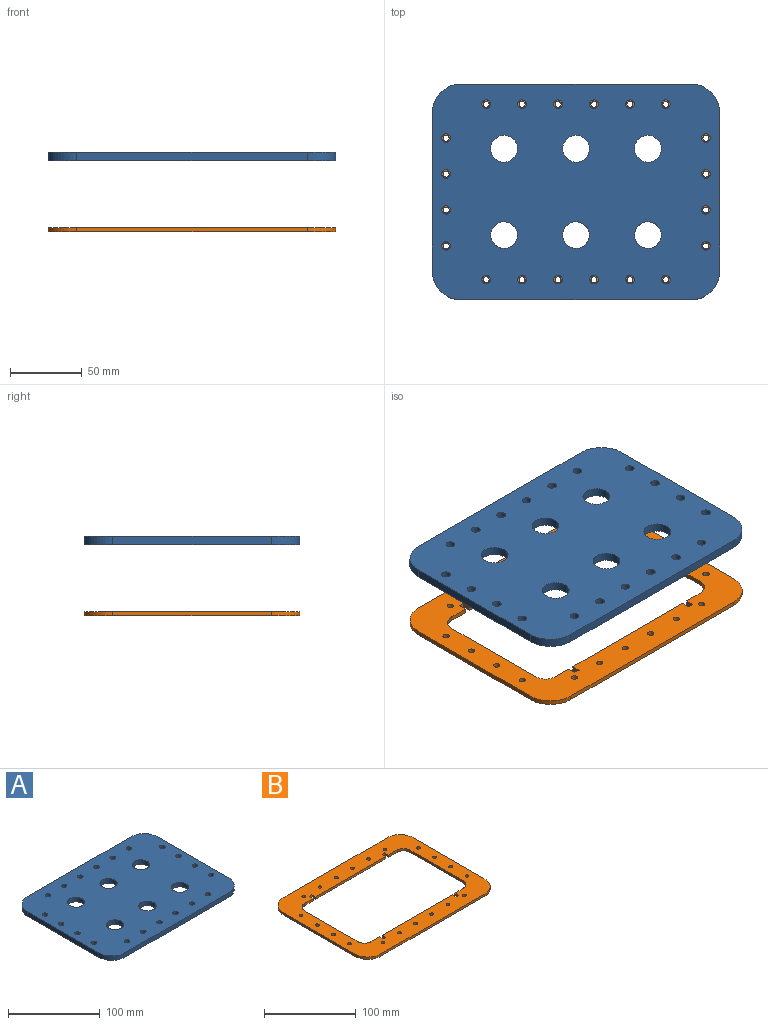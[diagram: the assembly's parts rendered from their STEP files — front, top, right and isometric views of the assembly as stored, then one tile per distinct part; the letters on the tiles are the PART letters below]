
ASSEMBLY  parts=2 mates=1
PART A: 36 faces, bbox 200x150x6 mm
  f0: cylinder r=20mm len=20mm, axis (0,0,1), area 188.5mm2, adj f1,f24,f34,f35
  f1: plane 110x6mm, normal (1,0,0), area 660mm2, adj f0,f2,f34,f35
  f2: cylinder r=20mm len=20mm, axis (0,0,1), area 188.5mm2, adj f1,f3,f34,f35
  f3: plane 160x6mm, normal (0,1,0), area 960mm2, adj f2,f4,f34,f35
  f4: cylinder r=20mm len=20mm, axis (0,0,1), area 188.5mm2, adj f3,f5,f34,f35
  f5: plane 110x6mm, normal (-1,0,0), area 660mm2, adj f4,f6,f34,f35
  f6: cylinder r=20mm len=20mm, axis (0,0,1), area 188.5mm2, adj f5,f24,f34,f35
  f7: cylinder r=3mm len=6mm, axis (0,0,1), area 113.1mm2, adj f34,f35
  f8: cylinder r=9.3mm len=18.6mm, axis (0,0,1), area 350.6mm2, adj f34,f35
  f9: cylinder r=3mm len=6mm, axis (0,0,1), area 113.1mm2, adj f34,f35
  f10: cylinder r=9.3mm len=18.6mm, axis (0,0,1), area 350.6mm2, adj f34,f35
  f11: cylinder r=9.3mm len=18.6mm, axis (0,0,1), area 350.6mm2, adj f34,f35
  f12: cylinder r=3mm len=6mm, axis (0,0,1), area 113.1mm2, adj f34,f35
  f13: cylinder r=3mm len=6mm, axis (0,0,1), area 113.1mm2, adj f34,f35
  f14: cylinder r=3mm len=6mm, axis (0,0,1), area 113.1mm2, adj f34,f35
  f15: cylinder r=3mm len=6mm, axis (0,0,1), area 113.1mm2, adj f34,f35
  f16: cylinder r=3mm len=6mm, axis (0,0,1), area 113.1mm2, adj f34,f35
  f17: cylinder r=3mm len=6mm, axis (0,0,1), area 113.1mm2, adj f34,f35
  f18: cylinder r=9.3mm len=18.6mm, axis (0,0,1), area 350.6mm2, adj f34,f35
  f19: cylinder r=3mm len=6mm, axis (0,0,1), area 113.1mm2, adj f34,f35
  f20: cylinder r=3mm len=6mm, axis (0,0,1), area 113.1mm2, adj f34,f35
  f21: cylinder r=3mm len=6mm, axis (0,0,1), area 113.1mm2, adj f34,f35
  f22: cylinder r=3mm len=6mm, axis (0,0,1), area 113.1mm2, adj f34,f35
  f23: cylinder r=3mm len=6mm, axis (0,0,1), area 113.1mm2, adj f34,f35
  f24: plane 160x6mm, normal (0,-1,0), area 960mm2, adj f0,f6,f34,f35
  f25: cylinder r=9.3mm len=18.6mm, axis (0,0,1), area 350.6mm2, adj f34,f35
  f26: cylinder r=3mm len=6mm, axis (0,0,1), area 113.1mm2, adj f34,f35
  f27: cylinder r=3mm len=6mm, axis (0,0,1), area 113.1mm2, adj f34,f35
  f28: cylinder r=3mm len=6mm, axis (0,0,1), area 113.1mm2, adj f34,f35
  f29: cylinder r=9.3mm len=18.6mm, axis (0,0,1), area 350.6mm2, adj f34,f35
  f30: cylinder r=3mm len=6mm, axis (0,0,1), area 113.1mm2, adj f34,f35
  f31: cylinder r=3mm len=6mm, axis (0,0,1), area 113.1mm2, adj f34,f35
  f32: cylinder r=3mm len=6mm, axis (0,0,1), area 113.1mm2, adj f34,f35
  f33: cylinder r=3mm len=6mm, axis (0,0,1), area 113.1mm2, adj f34,f35
  f34: plane 200x150mm, normal (0,0,1), area 27460.9mm2, adj f0,f1,f2,f3,f4,f5,f6,f7
  f35: plane 200x150mm, normal (0,0,-1), area 27460.9mm2, adj f0,f1,f2,f3,f4,f5,f6,f7
PART B: 54 faces, bbox 200x150x3 mm
  f0: plane 13x3mm, normal (0,1,0), area 39mm2, adj f1,f35,f52,f53
  f1: plane 6x3mm, normal (-1,0,0), area 18mm2, adj f0,f2,f52,f53
  f2: plane 4x3mm, normal (0,1,0), area 12mm2, adj f1,f3,f52,f53
  f3: plane 6x3mm, normal (1,0,0), area 18mm2, adj f2,f4,f52,f53
  f4: plane 108x3mm, normal (0,1,0), area 324mm2, adj f3,f5,f52,f53
  f5: plane 6x3mm, normal (-1,0,0), area 18mm2, adj f4,f6,f52,f53
  f6: plane 4x3mm, normal (0,1,0), area 12mm2, adj f5,f7,f52,f53
  f7: plane 6x3mm, normal (1,0,0), area 18mm2, adj f6,f8,f52,f53
  f8: plane 13x3mm, normal (0,1,0), area 39mm2, adj f7,f9,f52,f53
  f9: cylinder r=10mm len=10mm, axis (0,0,-1), area 47.1mm2, adj f8,f10,f52,f53
  f10: plane 81.95x3mm, normal (1,0,0), area 245.9mm2, adj f9,f11,f52,f53
  f11: cylinder r=10mm len=10mm, axis (0,0,-1), area 47.1mm2, adj f10,f12,f52,f53
  f12: plane 13x3mm, normal (0,-1,0), area 39mm2, adj f11,f13,f52,f53
  f13: plane 6x3mm, normal (1,0,0), area 18mm2, adj f12,f14,f52,f53
  f14: plane 4x3mm, normal (0,-1,0), area 12mm2, adj f13,f15,f52,f53
  f15: plane 6x3mm, normal (-1,0,0), area 18mm2, adj f14,f16,f52,f53
  f16: plane 108x3mm, normal (0,-1,0), area 324mm2, adj f15,f17,f52,f53
  f17: plane 6x3mm, normal (1,0,0), area 18mm2, adj f16,f18,f52,f53
  f18: plane 4x3mm, normal (0,-1,0), area 12mm2, adj f17,f19,f52,f53
  f19: plane 6x3mm, normal (-1,0,0), area 18mm2, adj f18,f20,f52,f53
  f20: plane 13x3mm, normal (0,-1,0), area 39mm2, adj f19,f21,f52,f53
  f21: cylinder r=10mm len=10mm, axis (0,0,-1), area 47.1mm2, adj f20,f22,f52,f53
  f22: plane 81.95x3mm, normal (-1,0,0), area 245.9mm2, adj f21,f35,f52,f53
  f23: plane 160x3mm, normal (0,-1,0), area 480mm2, adj f24,f36,f52,f53
  f24: cylinder r=20mm len=20mm, axis (0,0,-1), area 94.2mm2, adj f23,f25,f52,f53
  f25: plane 110x3mm, normal (1,0,0), area 330mm2, adj f24,f26,f52,f53
  f26: cylinder r=20mm len=20mm, axis (0,0,-1), area 94.2mm2, adj f25,f27,f52,f53
  f27: plane 160x3mm, normal (0,1,0), area 480mm2, adj f26,f28,f52,f53
  f28: cylinder r=20mm len=20mm, axis (0,0,-1), area 94.2mm2, adj f27,f29,f52,f53
  f29: plane 110x3mm, normal (-1,0,0), area 330mm2, adj f28,f36,f52,f53
  f30: cylinder r=2.1mm len=4.2mm, axis (0,0,-1), area 39.6mm2, adj f52,f53
  f31: cylinder r=2.1mm len=4.2mm, axis (0,0,-1), area 39.6mm2, adj f52,f53
  f32: cylinder r=2.1mm len=4.2mm, axis (0,0,-1), area 39.6mm2, adj f52,f53
  f33: cylinder r=2.1mm len=4.2mm, axis (0,0,-1), area 39.6mm2, adj f52,f53
  f34: cylinder r=2.1mm len=4.2mm, axis (0,0,-1), area 39.6mm2, adj f52,f53
  f35: cylinder r=10mm len=10mm, axis (0,0,-1), area 47.1mm2, adj f0,f22,f52,f53
  f36: cylinder r=20mm len=20mm, axis (0,0,-1), area 94.2mm2, adj f23,f29,f52,f53
  f37: cylinder r=2.1mm len=4.2mm, axis (0,0,-1), area 39.6mm2, adj f52,f53
  f38: cylinder r=2.1mm len=4.2mm, axis (0,0,-1), area 39.6mm2, adj f52,f53
  f39: cylinder r=2.1mm len=4.2mm, axis (0,0,-1), area 39.6mm2, adj f52,f53
  f40: cylinder r=2.1mm len=4.2mm, axis (0,0,-1), area 39.6mm2, adj f52,f53
  f41: cylinder r=2.1mm len=4.2mm, axis (0,0,-1), area 39.6mm2, adj f52,f53
  f42: cylinder r=2.1mm len=4.2mm, axis (0,0,-1), area 39.6mm2, adj f52,f53
  f43: cylinder r=2.1mm len=4.2mm, axis (0,0,-1), area 39.6mm2, adj f52,f53
  f44: cylinder r=2.1mm len=4.2mm, axis (0,0,-1), area 39.6mm2, adj f52,f53
  f45: cylinder r=2.1mm len=4.2mm, axis (0,0,-1), area 39.6mm2, adj f52,f53
  f46: cylinder r=2.1mm len=4.2mm, axis (0,0,-1), area 39.6mm2, adj f52,f53
  f47: cylinder r=2.1mm len=4.2mm, axis (0,0,-1), area 39.6mm2, adj f52,f53
  f48: cylinder r=2.1mm len=4.2mm, axis (0,0,-1), area 39.6mm2, adj f52,f53
  f49: cylinder r=2.1mm len=4.2mm, axis (0,0,-1), area 39.6mm2, adj f52,f53
  f50: cylinder r=2.1mm len=4.2mm, axis (0,0,-1), area 39.6mm2, adj f52,f53
  f51: cylinder r=2.1mm len=4.2mm, axis (0,0,-1), area 39.6mm2, adj f52,f53
  f52: plane 200x150mm, normal (0,0,1), area 12853mm2, adj f0,f1,f2,f3,f4,f5,f6,f7
  f53: plane 200x150mm, normal (0,0,-1), area 12853mm2, adj f0,f1,f2,f3,f4,f5,f6,f7
PLACE A t=(-26.52,18.82,9.43)mm
PLACE B t=(-26.52,18.87,0)mm
MATE slider A.f31 <-> B.f50  axis (0,0,1) through (35.98,-117.13,55.43)mm
